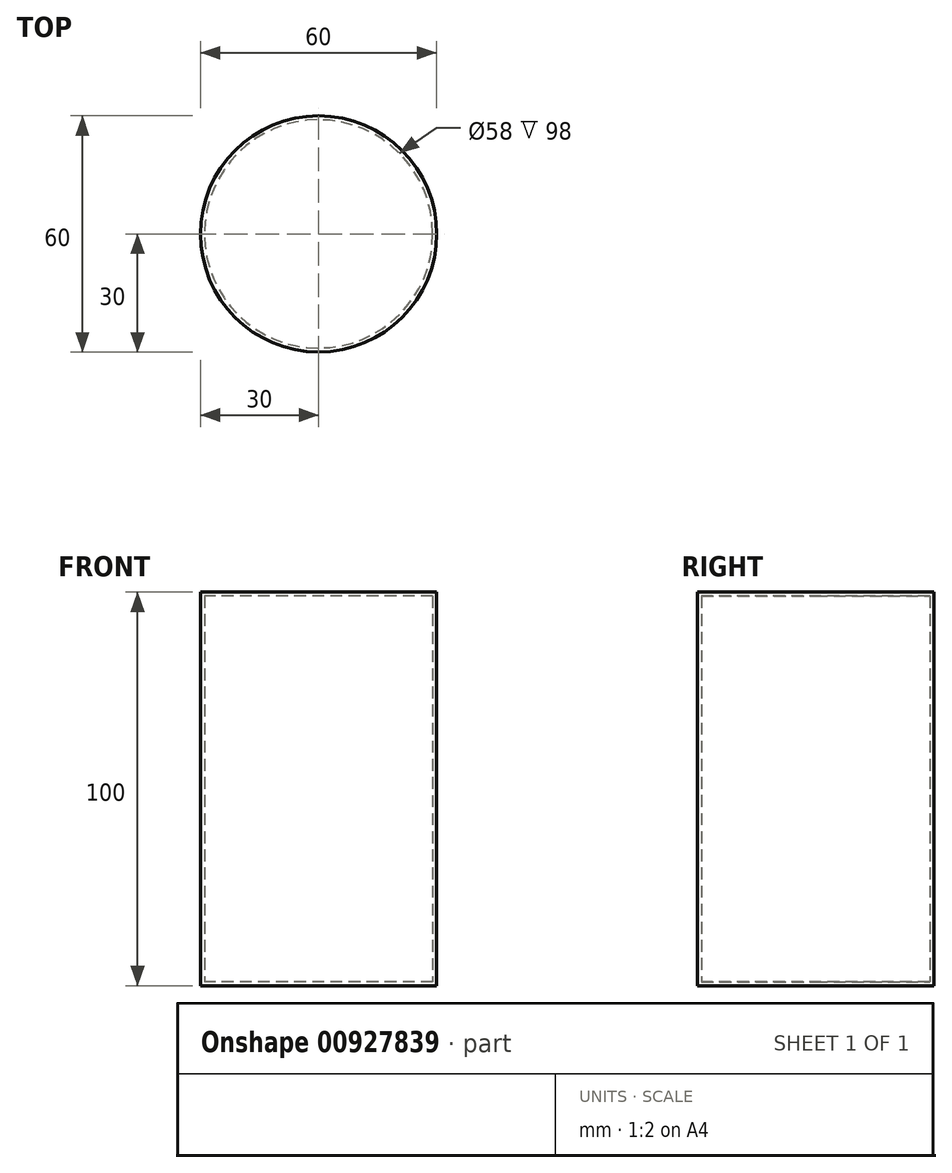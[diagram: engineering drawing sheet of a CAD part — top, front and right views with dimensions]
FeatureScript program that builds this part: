
annotation { "Feature Type Name" : "Feature", "Feature Type Description" : "" }
export const myFeature = defineFeature(function(context is Context, id is Id, definition is map)
    precondition{}
    {
        {
            var Q0;
            Q0=qCreatedBy(makeId("Top.planeOp"),FACE);
            var sketch = newSketch(context, id + "F0", { "sketchPlane" : qUnion([Q0])});
            skCircle(sketch, "E0", {"center": v(0, 0) * mm, "radius": 30 * mm});
            skSolve(sketch);
        }
        {
            var Q0;
            Q0 = qSketchRegion(id + "F0", true);
            extrude(context, id + "F1", {"entities" : qUnion([Q0]), "endBound" : BoundingType.SYMMETRIC, "depth" : 100 * mm, "offsetDistance" : 25 * mm});
        }
        {
            var Q0;
            Q0=makeQuery(id+"F1.opExtrude","CAP_FACE",FACE,{"disambiguationData":[OSD([sQuery(id+"F0.wireOp",EDGE,"E0")])],"isStart":false});
            shell(context, id + "F2", {"entities" : qUnion([Q0]), "thickness" : 1 * mm});
        }
        {
            var Q0;
            Q0=makeQuery(id+"F1.opExtrude","CAP_FACE",FACE,{"disambiguationData":[OSD([sQuery(id+"F0.wireOp",EDGE,"E0")])],"isStart":false});
            var sketch = newSketch(context, id + "F3", { "sketchPlane" : qUnion([Q0])});
            skCircle(sketch, "E1", {"center": v(0, 0) * mm, "radius": 30 * mm});
            skSolve(sketch);
        }
        {
            var Q0;
            Q0 = qSketchRegion(id + "F3", true);
            extrude(context, id + "F4", {"entities" : qUnion([Q0]), "operationType" : NewBodyOperationType.ADD, "oppositeDirection" : true, "depth" : 1 * mm, "offsetDistance" : 25 * mm});
        }
    });
